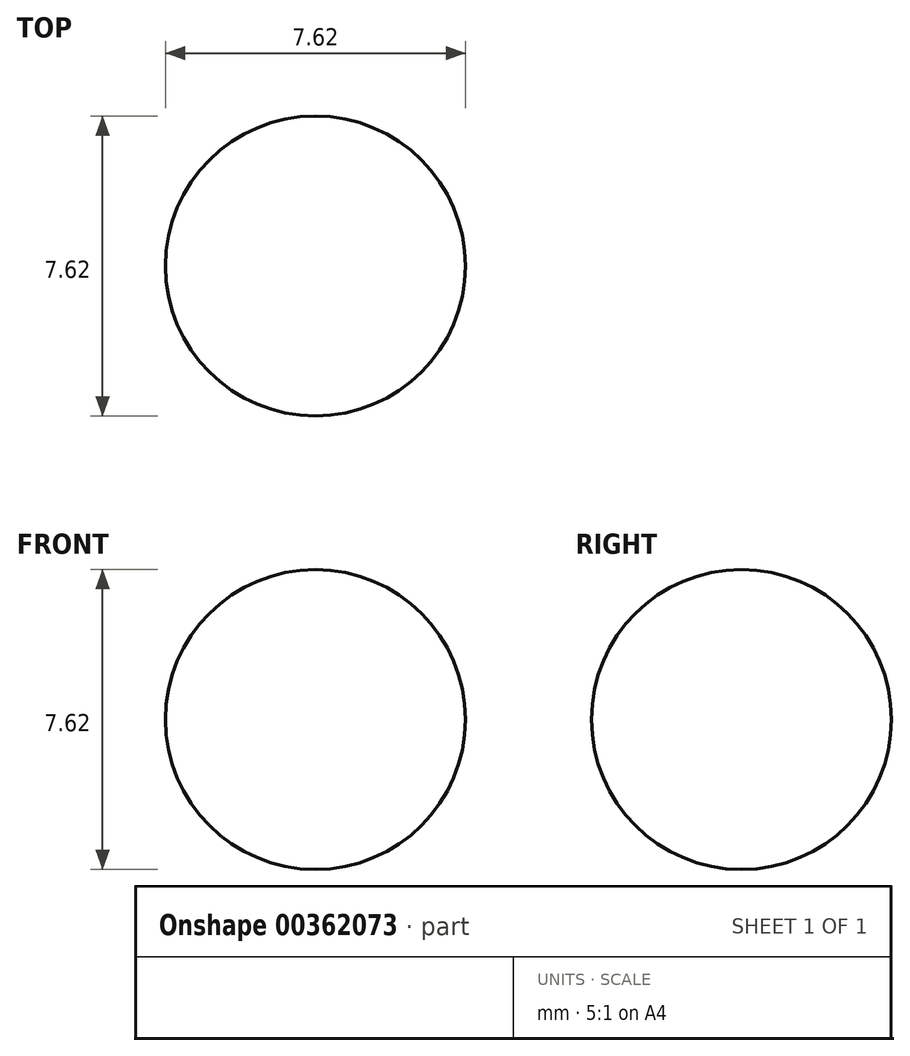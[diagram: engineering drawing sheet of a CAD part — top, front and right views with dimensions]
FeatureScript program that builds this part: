
annotation { "Feature Type Name" : "Feature", "Feature Type Description" : "" }
export const myFeature = defineFeature(function(context is Context, id is Id, definition is map)
    precondition{}
    {
        {
            var Q0;
            Q0=qCreatedBy(makeId("Front.planeOp"),FACE);
            var sketch = newSketch(context, id + "F0", { "sketchPlane" : qUnion([Q0])});
            skArc(sketch, "E0", {"start": v(0.6, 3.81) * mm, "mid": v(-3.2, 0) * mm, "end": v(0.6, -3.81) * mm});
            skPoint(sketch, "E1", {"position": v(0.6, 3.81) * mm});
            skPoint(sketch, "E2", {"position": v(0.6, -3.81) * mm});
            skLineSegment(sketch, "E3", {"start": v(0.6, 3.81) * mm, "end": v(0.6, -3.81) * mm});
            skSolve(sketch);
        }
        {
            var Q0;
            Q0=makeQuery(id+"F0.imprint","IMPRINT",FACE,{"disambiguationData":[TD([[makeQuery(id+"F0.imprint","IMPRINT",EDGE,{"derivedFrom":sQuery(id+"F0.wireOp",EDGE,"E0")}),1.0]])]});
            var Q1;
            Q1=sQuery(id+"F0.wireOp",EDGE,"E3");
            revolve(context, id + "F1", {"entities" : qUnion([Q0]), "axis" : qUnion([Q1]), "revolveType" : RevolveType.FULL});
        }
    });
